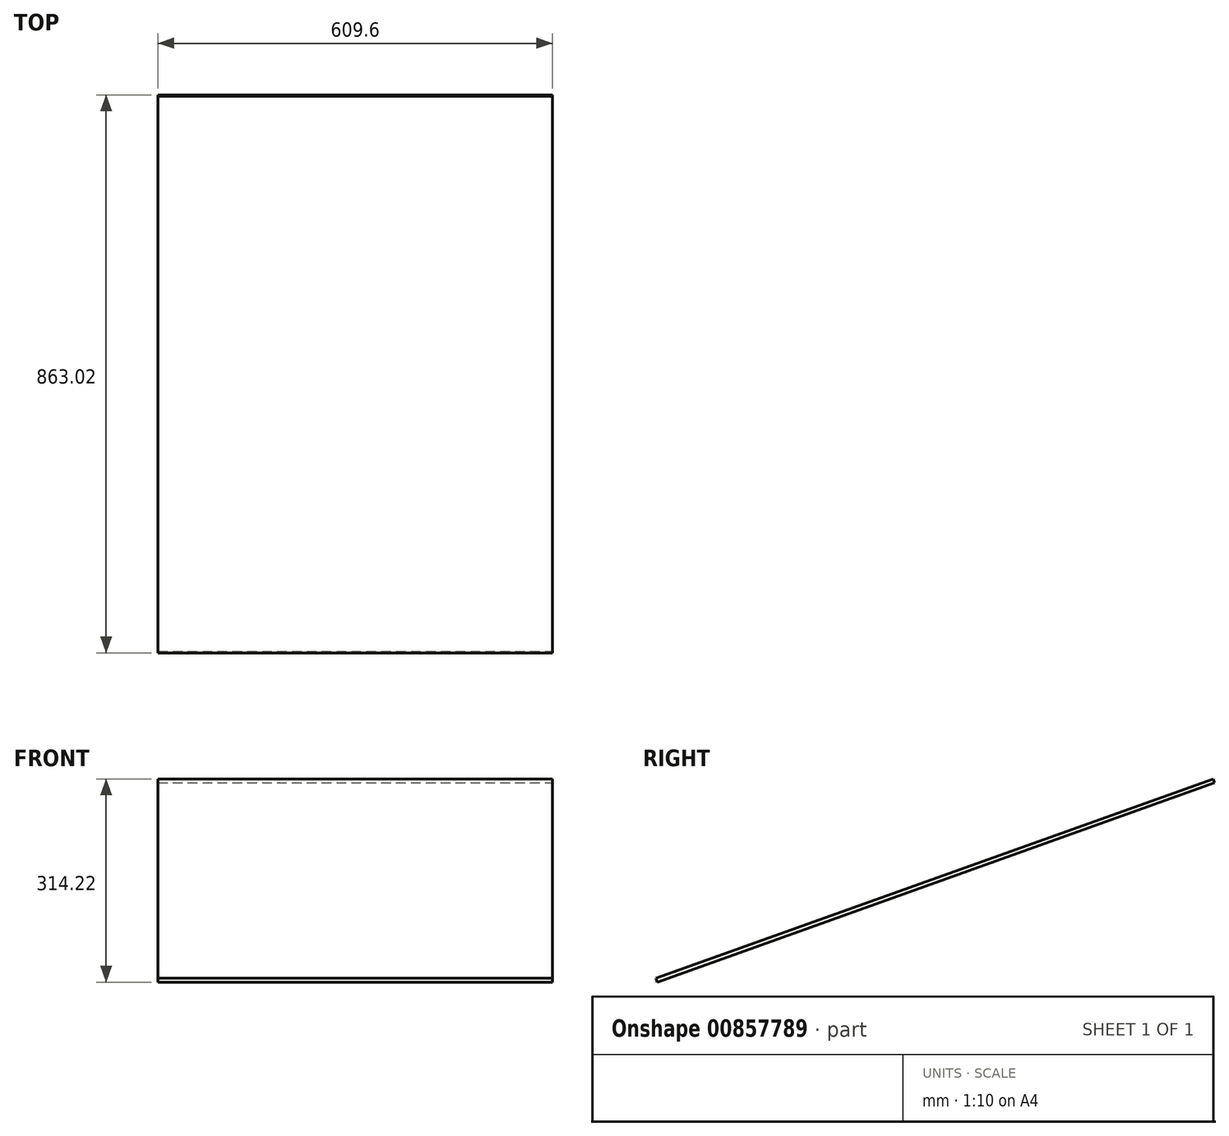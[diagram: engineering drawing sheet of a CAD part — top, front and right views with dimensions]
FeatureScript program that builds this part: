
annotation { "Feature Type Name" : "Feature", "Feature Type Description" : "" }
export const myFeature = defineFeature(function(context is Context, id is Id, definition is map)
    precondition{}
    {
        {
            var Q0;
            Q0=qCreatedBy(makeId("Top.planeOp"),FACE);
            var sketch = newSketch(context, id + "F0", { "sketchPlane" : qUnion([Q0])});
            skLineSegment(sketch, "E0.bottom", {"start": v(-304.8, 914.4) * mm, "end": v(304.8, 914.4) * mm});
            skLineSegment(sketch, "E0.top", {"start": v(-304.8, 0) * mm, "end": v(304.8, 0) * mm});
            skLineSegment(sketch, "E0.left", {"start": v(-304.8, 914.4) * mm, "end": v(-304.8, 0) * mm});
            skLineSegment(sketch, "E0.right", {"start": v(304.8, 914.4) * mm, "end": v(304.8, 0) * mm});
            skSolve(sketch);
        }
        {
            var Q0;
            Q0 = qSketchRegion(id + "F0", true);
            extrude(context, id + "F1", {"entities" : qUnion([Q0]), "depth" : 6.35 * mm, "offsetDistance" : 25.4 * mm});
        }
        {
            var Q0;
            Q0=makeQuery(id+"F1.opExtrude","SWEPT_BODY",BODY,{"disambiguationData":[OSD([sQuery(id+"F0.wireOp",EDGE,"E0.bottom"),sQuery(id+"F0.wireOp",EDGE,"E0.top"),sQuery(id+"F0.wireOp",EDGE,"E0.left"),sQuery(id+"F0.wireOp",EDGE,"E0.right")])]});
            var Q1;
            Q1=makeQuery(id+"F1.opExtrude","CAP_EDGE",EDGE,{"disambiguationData":[OSD([sQuery(id+"F0.wireOp",EDGE,"E0.top")])],"isStart":true});
            transform(context, id + "F2", {"entities" : qUnion([Q0]), "transformType" : TransformType.ROTATION, "transformAxis" : qUnion([Q1]), "angle" : 19.7 * degree, "makeCopy" : false});
        }
    });
